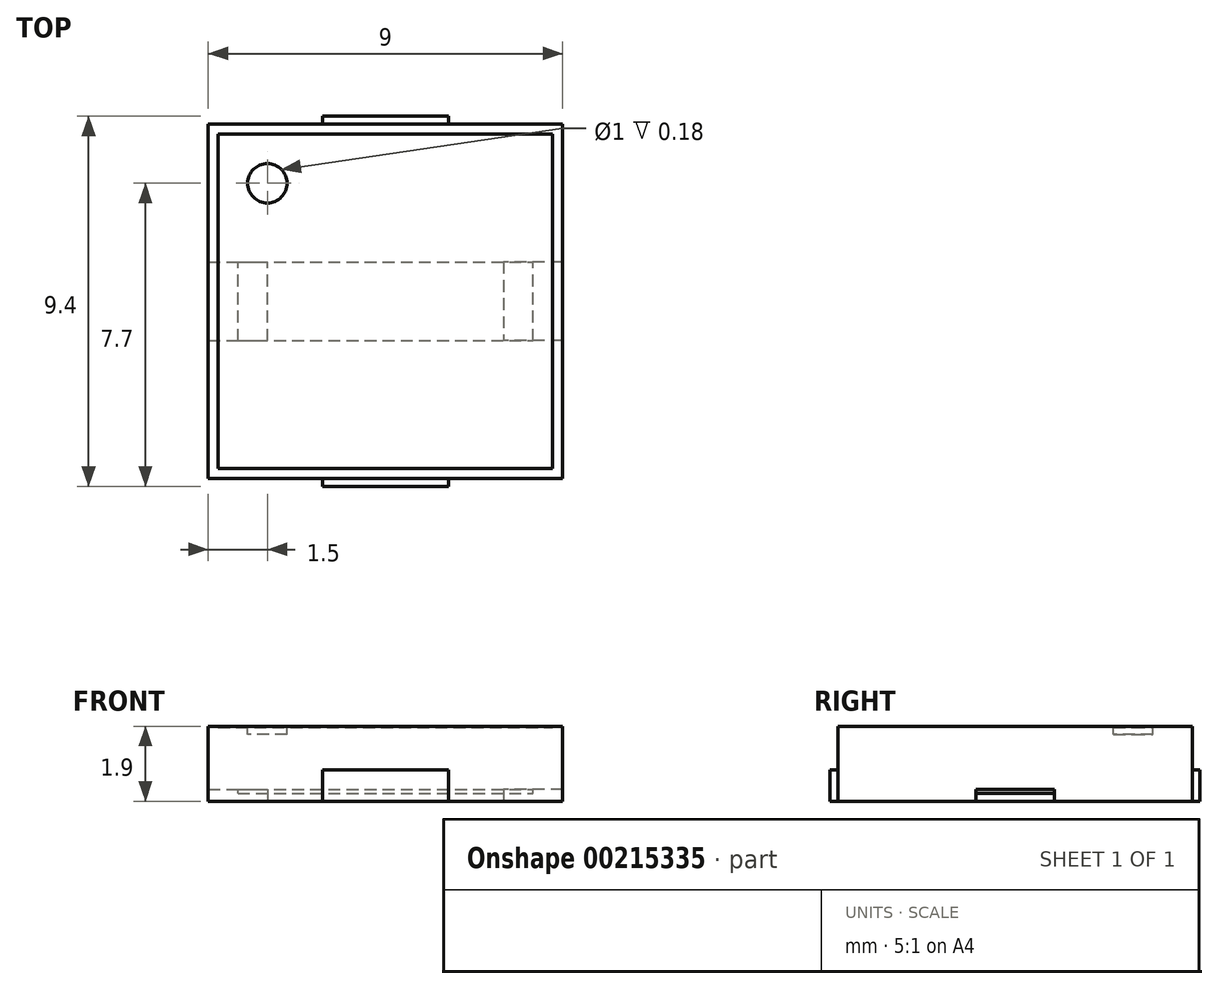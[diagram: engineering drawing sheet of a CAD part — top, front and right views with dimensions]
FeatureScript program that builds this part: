
annotation { "Feature Type Name" : "Feature", "Feature Type Description" : "" }
export const myFeature = defineFeature(function(context is Context, id is Id, definition is map)
    precondition{}
    {
        {
            var Q0;
            Q0=qCreatedBy(makeId("Top.planeOp"),FACE);
            var sketch = newSketch(context, id + "F0", { "sketchPlane" : qUnion([Q0])});
            skLineSegment(sketch, "E0.bottom", {"start": v(-4.5, 4.5) * mm, "end": v(-1.6, 4.5) * mm});
            skLineSegment(sketch, "E0.top", {"start": v(-4.5, -4.5) * mm, "end": v(-1.6, -4.5) * mm});
            skLineSegment(sketch, "E0.left", {"start": v(-4.5, 4.5) * mm, "end": v(-4.5, -4.5) * mm});
            skLineSegment(sketch, "E0.right", {"start": v(4.5, 4.5) * mm, "end": v(4.5, -4.5) * mm});
            skPoint(sketch, "E0.middle", {"position": v(0, 0) * mm});
            skPoint(sketch, "E1.middle", {"position": v(0, -2) * mm});
            skLineSegment(sketch, "E2.top", {"start": v(-1.6, 3.5) * mm, "end": v(1.6, 3.5) * mm});
            skLineSegment(sketch, "E2.left", {"start": v(-1.6, 4.5) * mm, "end": v(-1.6, 3.5) * mm});
            skLineSegment(sketch, "E2.right", {"start": v(1.6, 4.5) * mm, "end": v(1.6, 3.5) * mm});
            skPoint(sketch, "E2.middle", {"position": v(0, 4) * mm});
            skLineSegment(sketch, "E3.top", {"start": v(-1.6, -3.5) * mm, "end": v(1.6, -3.5) * mm});
            skLineSegment(sketch, "E3.left", {"start": v(-1.6, -4.5) * mm, "end": v(-1.6, -3.5) * mm});
            skLineSegment(sketch, "E3.right", {"start": v(1.6, -4.5) * mm, "end": v(1.6, -3.5) * mm});
            skPoint(sketch, "E3.middle", {"position": v(0, -4) * mm});
            skPoint(sketch, "E1.bottom.start.orphan", {"position": v(-2.5, -2.85) * mm});
            skPoint(sketch, "E1.right.start.orphan", {"position": v(2.5, -2.85) * mm});
            skPoint(sketch, "E1.top.end.orphan", {"position": v(2.5, -1.14) * mm});
            skPoint(sketch, "E1.top.start.orphan", {"position": v(-2.5, -1.14) * mm});
            skLineSegment(sketch, "E4.trimOffspring", {"start": v(1.6, 4.5) * mm, "end": v(4.5, 4.5) * mm});
            skLineSegment(sketch, "E5.trimOffspring", {"start": v(1.6, -4.5) * mm, "end": v(4.5, -4.5) * mm});
            skSolve(sketch);
        }
        {
            var Q0;
            Q0 = qSketchRegion(id + "F0", true);
            extrude(context, id + "F1", {"entities" : qUnion([Q0]), "depth" : 1.9 * mm});
        }
        {
            var Q0;
            Q0=makeQuery(id+"F1.opExtrude","CAP_FACE",FACE,{"disambiguationData":[OSD([sQuery(id+"F0.wireOp",EDGE,"E0.bottom"),sQuery(id+"F0.wireOp",EDGE,"E0.top"),sQuery(id+"F0.wireOp",EDGE,"E0.left"),sQuery(id+"F0.wireOp",EDGE,"E0.right")])],"isStart":false});
            var sketch = newSketch(context, id + "F2", { "sketchPlane" : qUnion([Q0])});
            skCircle(sketch, "E6", {"center": v(-3, 3) * mm, "radius": 0.5 * mm});
            skSolve(sketch);
        }
        {
            var Q0;
            Q0 = qSketchRegion(id + "F2", true);
            extrude(context, id + "F3", {"entities" : qUnion([Q0]), "operationType" : NewBodyOperationType.REMOVE, "oppositeDirection" : true, "depth" : 0.2 * mm});
        }
        {
            var Q0;
            Q0=makeQuery(id+"F1.opExtrude","CAP_FACE",FACE,{"disambiguationData":[OSD([sQuery(id+"F0.wireOp",EDGE,"E0.bottom"),sQuery(id+"F0.wireOp",EDGE,"E0.top"),sQuery(id+"F0.wireOp",EDGE,"E0.left"),sQuery(id+"F0.wireOp",EDGE,"E0.right")])],"isStart":true});
            var sketch = newSketch(context, id + "F4", { "sketchPlane" : qUnion([Q0])});
            skLineSegment(sketch, "E7.left", {"start": v(-1.6, 4.5) * mm, "end": v(-1.6, 3.5) * mm});
            skLineSegment(sketch, "E7.right", {"start": v(1.6, 4.5) * mm, "end": v(1.6, 3.5) * mm});
            skPoint(sketch, "E7.middle", {"position": v(0, 0) * mm});
            skLineSegment(sketch, "E8.top", {"start": v(-1.6, 3.5) * mm, "end": v(1.6, 3.5) * mm});
            skLineSegment(sketch, "E9.top", {"start": v(1.6, -3.5) * mm, "end": v(-1.6, -3.5) * mm});
            skLineSegment(sketch, "E9.left", {"start": v(1.6, -4.5) * mm, "end": v(1.6, -3.5) * mm});
            skLineSegment(sketch, "E9.right", {"start": v(-1.6, -4.5) * mm, "end": v(-1.6, -3.5) * mm});
            skLineSegment(sketch, "E10.trimOffspring", {"start": v(-1.6, -3.5) * mm, "end": v(-1.6, -4.5) * mm});
            skLineSegment(sketch, "E11.trimOffspring", {"start": v(1.6, -3.5) * mm, "end": v(1.6, -4.5) * mm});
            skLineSegment(sketch, "E12.top", {"start": v(1.6, 4.7) * mm, "end": v(-1.6, 4.7) * mm});
            skLineSegment(sketch, "E12.left", {"start": v(1.6, 4.5) * mm, "end": v(1.6, 4.7) * mm});
            skLineSegment(sketch, "E12.right", {"start": v(-1.6, 4.5) * mm, "end": v(-1.6, 4.7) * mm});
            skLineSegment(sketch, "E13.top", {"start": v(-1.6, -4.7) * mm, "end": v(1.6, -4.7) * mm});
            skLineSegment(sketch, "E13.left", {"start": v(-1.6, -4.5) * mm, "end": v(-1.6, -4.7) * mm});
            skLineSegment(sketch, "E13.right", {"start": v(1.6, -4.5) * mm, "end": v(1.6, -4.7) * mm});
            skSolve(sketch);
        }
        {
            var Q0;
            Q0 = qSketchRegion(id + "F4", true);
            extrude(context, id + "F5", {"entities" : qUnion([Q0]), "oppositeDirection" : true, "depth" : 0.8 * mm});
        }
        {
            var Q0;
            Q0=makeQuery(id+"F1.opExtrude","CAP_FACE",FACE,{"disambiguationData":[OSD([sQuery(id+"F0.wireOp",EDGE,"E0.bottom"),sQuery(id+"F0.wireOp",EDGE,"E0.top"),sQuery(id+"F0.wireOp",EDGE,"E0.left"),sQuery(id+"F0.wireOp",EDGE,"E0.right"),sQuery(id+"F0.wireOp",EDGE,"E2.top"),sQuery(id+"F0.wireOp",EDGE,"E2.left"),sQuery(id+"F0.wireOp",EDGE,"E2.right"),sQuery(id+"F0.wireOp",EDGE,"E3.top"),sQuery(id+"F0.wireOp",EDGE,"E3.left"),sQuery(id+"F0.wireOp",EDGE,"E3.right"),sQuery(id+"F0.wireOp",EDGE,"E4.trimOffspring"),sQuery(id+"F0.wireOp",EDGE,"E5.trimOffspring")])],"isStart":false});
            var sketch = newSketch(context, id + "F6", { "sketchPlane" : qUnion([Q0])});
            skLineSegment(sketch, "E14.bottom", {"start": v(1.6, 3.5) * mm, "end": v(-1.6, 3.5) * mm});
            skLineSegment(sketch, "E14.top", {"start": v(1.6, 4.5) * mm, "end": v(-1.6, 4.5) * mm});
            skLineSegment(sketch, "E14.left", {"start": v(1.6, 3.5) * mm, "end": v(1.6, 4.5) * mm});
            skLineSegment(sketch, "E14.right", {"start": v(-1.6, 3.5) * mm, "end": v(-1.6, 4.5) * mm});
            skLineSegment(sketch, "E15.bottom", {"start": v(-1.6, -3.5) * mm, "end": v(1.6, -3.5) * mm});
            skLineSegment(sketch, "E15.top", {"start": v(-1.6, -4.5) * mm, "end": v(1.6, -4.5) * mm});
            skLineSegment(sketch, "E15.left", {"start": v(-1.6, -3.5) * mm, "end": v(-1.6, -4.5) * mm});
            skLineSegment(sketch, "E15.right", {"start": v(1.6, -3.5) * mm, "end": v(1.6, -4.5) * mm});
            skSolve(sketch);
        }
        {
            var Q0;
            Q0 = qSketchRegion(id + "F6", true);
            extrude(context, id + "F7", {"entities" : qUnion([Q0]), "operationType" : NewBodyOperationType.ADD, "oppositeDirection" : true, "depth" : 1.2 * mm});
        }
        {
            var Q0;
            Q0=makeQuery(id+"F1.opExtrude","CAP_FACE",FACE,{"disambiguationData":[OSD([sQuery(id+"F0.wireOp",EDGE,"E0.bottom"),sQuery(id+"F0.wireOp",EDGE,"E0.top"),sQuery(id+"F0.wireOp",EDGE,"E0.left"),sQuery(id+"F0.wireOp",EDGE,"E0.right"),sQuery(id+"F0.wireOp",EDGE,"E2.top"),sQuery(id+"F0.wireOp",EDGE,"E2.left"),sQuery(id+"F0.wireOp",EDGE,"E2.right"),sQuery(id+"F0.wireOp",EDGE,"E3.top"),sQuery(id+"F0.wireOp",EDGE,"E3.left"),sQuery(id+"F0.wireOp",EDGE,"E3.right"),sQuery(id+"F0.wireOp",EDGE,"E4.trimOffspring"),sQuery(id+"F0.wireOp",EDGE,"E5.trimOffspring")])],"isStart":true});
            var sketch = newSketch(context, id + "F8", { "sketchPlane" : qUnion([Q0])});
            skLineSegment(sketch, "E16.bottom", {"start": v(-4.5, 1) * mm, "end": v(-3, 1) * mm});
            skLineSegment(sketch, "E16.top", {"start": v(-4.5, -1) * mm, "end": v(-3, -1) * mm});
            skLineSegment(sketch, "E16.left", {"start": v(-4.5, 1) * mm, "end": v(-4.5, -1) * mm});
            skLineSegment(sketch, "E16.right", {"start": v(-3, 1) * mm, "end": v(-3, -1) * mm});
            skPoint(sketch, "E16.middle", {"position": v(-3.75, 0) * mm});
            skLineSegment(sketch, "E17.bottom", {"start": v(4.5, -1) * mm, "end": v(3, -1) * mm});
            skLineSegment(sketch, "E17.top", {"start": v(4.5, 1) * mm, "end": v(3, 1) * mm});
            skLineSegment(sketch, "E17.left", {"start": v(4.5, -1) * mm, "end": v(4.5, 1) * mm});
            skLineSegment(sketch, "E17.right", {"start": v(3, -1) * mm, "end": v(3, 1) * mm});
            skPoint(sketch, "E17.middle", {"position": v(3.75, 0) * mm});
            skSolve(sketch);
        }
        {
            var Q0;
            Q0 = qSketchRegion(id + "F8", true);
            extrude(context, id + "F9", {"entities" : qUnion([Q0]), "operationType" : NewBodyOperationType.REMOVE, "oppositeDirection" : true, "depth" : 0.3 * mm});
        }
        {
            var Q0;
            Q0=makeQuery(id+"F9.boolean.opBoolean","COPY",FACE,{"derivedFrom":makeQuery(id+"F9.opExtrude","CAP_FACE",FACE,{"disambiguationData":[OSD([sQuery(id+"F8.wireOp",EDGE,"E16.bottom"),sQuery(id+"F8.wireOp",EDGE,"E16.top"),sQuery(id+"F8.wireOp",EDGE,"E16.left"),sQuery(id+"F8.wireOp",EDGE,"E16.right")])],"isStart":false})});
            var sketch = newSketch(context, id + "F10", { "sketchPlane" : qUnion([Q0])});
            skLineSegment(sketch, "E18.bottom", {"start": v(-3.75, 1) * mm, "end": v(3.75, 1) * mm});
            skLineSegment(sketch, "E18.top", {"start": v(-3.75, -1) * mm, "end": v(3.75, -1) * mm});
            skLineSegment(sketch, "E18.left", {"start": v(-3.75, 1) * mm, "end": v(-3.75, -1) * mm});
            skLineSegment(sketch, "E18.right", {"start": v(3.75, 1) * mm, "end": v(3.75, -1) * mm});
            skPoint(sketch, "E18.middle", {"position": v(0, 0) * mm});
            skSolve(sketch);
        }
        {
            var Q0;
            Q0 = qSketchRegion(id + "F10", true);
            extrude(context, id + "F11", {"entities" : qUnion([Q0]), "depth" : 0.1 * mm});
        }
        {
            var Q0;
            Q0=makeQuery(id+"F7.boolean.opBoolean","MERGE",FACE,{"derivedFrom":[makeQuery(id+"F1.opExtrude","CAP_FACE",FACE,{"disambiguationData":[OSD([sQuery(id+"F0.wireOp",EDGE,"E0.bottom"),sQuery(id+"F0.wireOp",EDGE,"E0.top"),sQuery(id+"F0.wireOp",EDGE,"E0.left"),sQuery(id+"F0.wireOp",EDGE,"E0.right"),sQuery(id+"F0.wireOp",EDGE,"E2.top"),sQuery(id+"F0.wireOp",EDGE,"E2.left"),sQuery(id+"F0.wireOp",EDGE,"E2.right"),sQuery(id+"F0.wireOp",EDGE,"E3.top"),sQuery(id+"F0.wireOp",EDGE,"E3.left"),sQuery(id+"F0.wireOp",EDGE,"E3.right"),sQuery(id+"F0.wireOp",EDGE,"E4.trimOffspring"),sQuery(id+"F0.wireOp",EDGE,"E5.trimOffspring")])],"isStart":false}),makeQuery(id+"F7.opExtrude","CAP_FACE",FACE,{"disambiguationData":[OSD([sQuery(id+"F6.wireOp",EDGE,"E14.bottom"),sQuery(id+"F6.wireOp",EDGE,"E14.top"),sQuery(id+"F6.wireOp",EDGE,"E14.left"),sQuery(id+"F6.wireOp",EDGE,"E14.right")])],"isStart":true}),makeQuery(id+"F7.opExtrude","CAP_FACE",FACE,{"disambiguationData":[OSD([sQuery(id+"F6.wireOp",EDGE,"E15.bottom"),sQuery(id+"F6.wireOp",EDGE,"E15.top"),sQuery(id+"F6.wireOp",EDGE,"E15.left"),sQuery(id+"F6.wireOp",EDGE,"E15.right")])],"isStart":true})]});
            var sketch = newSketch(context, id + "F12", { "sketchPlane" : qUnion([Q0])});
            skLineSegment(sketch, "E19.bottom", {"start": v(-4.25, 4.25) * mm, "end": v(4.25, 4.25) * mm});
            skLineSegment(sketch, "E19.top", {"start": v(-4.25, -4.25) * mm, "end": v(4.25, -4.25) * mm});
            skLineSegment(sketch, "E19.left", {"start": v(-4.25, 4.25) * mm, "end": v(-4.25, -4.25) * mm});
            skLineSegment(sketch, "E19.right", {"start": v(4.25, 4.25) * mm, "end": v(4.25, -4.25) * mm});
            skPoint(sketch, "E19.middle", {"position": v(0, 0) * mm});
            skSolve(sketch);
        }
        {
            var Q0;
            Q0 = qSketchRegion(id + "F12", true);
            extrude(context, id + "F13", {"entities" : qUnion([Q0]), "operationType" : NewBodyOperationType.REMOVE, "oppositeDirection" : true, "depth" : 0.02 * mm});
        }
    });
